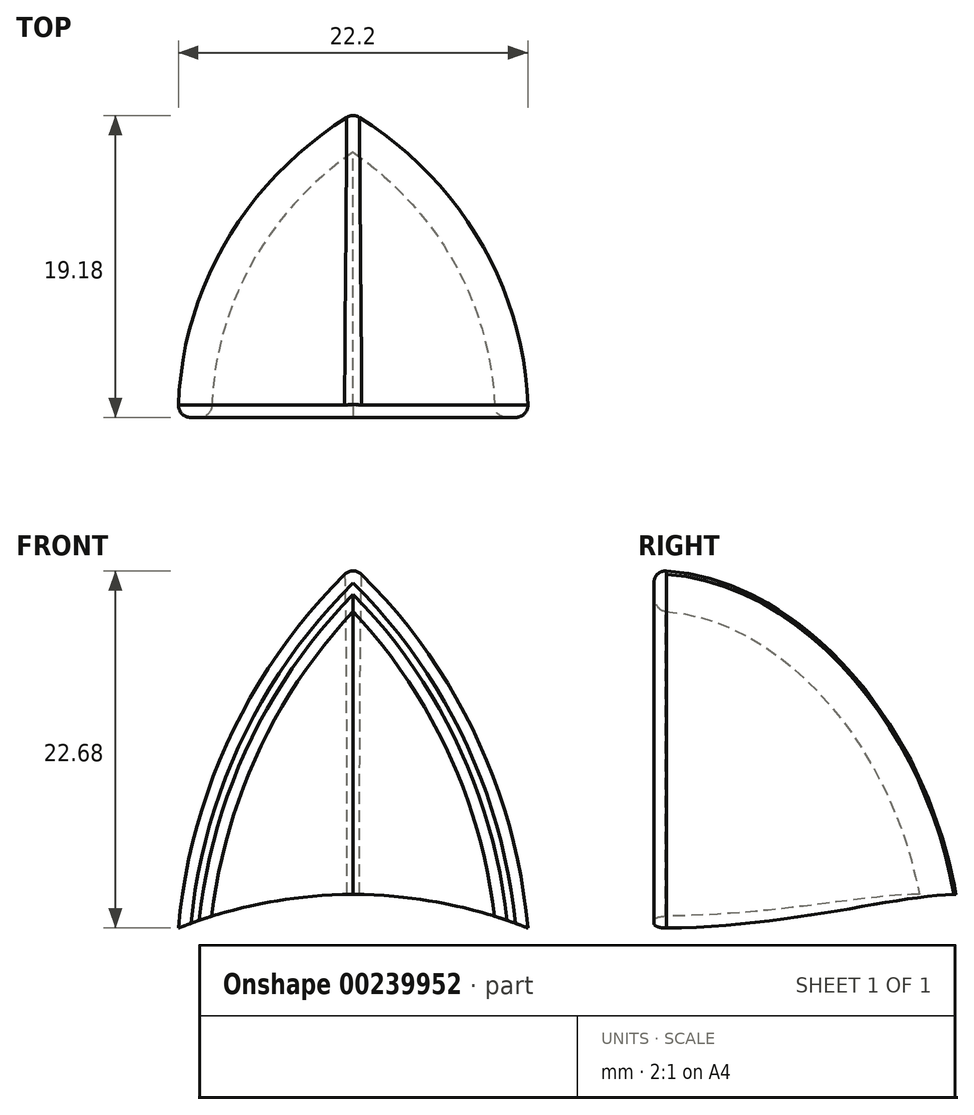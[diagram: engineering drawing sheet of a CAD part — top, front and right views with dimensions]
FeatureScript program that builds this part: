
annotation { "Feature Type Name" : "Feature", "Feature Type Description" : "" }
export const myFeature = defineFeature(function(context is Context, id is Id, definition is map)
    precondition{}
    {
        {
            var Q0;
            Q0=qCreatedBy(makeId("Front.planeOp"),FACE);
            var sketch = newSketch(context, id + "F0", { "sketchPlane" : qUnion([Q0])});
            skArc(sketch, "E0", {"start": v(22.86, 0) * mm, "mid": v(15.77, 18.5) * mm, "end": v(0, 30.48) * mm});
            skArc(sketch, "E1.0", {"start": v(20.82, 0) * mm, "mid": v(14.33, 17.03) * mm, "end": v(0, 28.29) * mm});
            skLineSegment(sketch, "E2", {"start": v(20.82, 0) * mm, "end": v(22.86, 0) * mm});
            skLineSegment(sketch, "E3", {"start": v(0, 28.29) * mm, "end": v(0, 30.48) * mm});
            skSolve(sketch);
        }
        {
            var Q0;
            Q0=makeQuery(id+"F0.imprint","IMPRINT",FACE,{"disambiguationData":[TD([[makeQuery(id+"F0.imprint","IMPRINT",EDGE,{"derivedFrom":sQuery(id+"F0.wireOp",EDGE,"E0")}),1.0]])]});
            var Q1;
            Q1=sQuery(id+"F0.wireOp",EDGE,"E3");
            revolve(context, id + "F1", {"entities" : qUnion([Q0]), "axis" : qUnion([Q1]), "revolveType" : RevolveType.ONE_DIRECTION, "angle" : 70 * degree});
        }
        {
            var Q0;
            Q0=makeQuery(id+"F1.opRevolve","CAP_FACE",FACE,{"disambiguationData":[OSD([sQuery(id+"F0.wireOp",EDGE,"E0"),sQuery(id+"F0.wireOp",EDGE,"E1.0"),sQuery(id+"F0.wireOp",EDGE,"E2"),sQuery(id+"F0.wireOp",EDGE,"E3")])],"isStart":true});
            var sketch = newSketch(context, id + "F2", { "sketchPlane" : qUnion([Q0])});
            skLineSegment(sketch, "E4.bottom", {"start": v(11.75, -2.07) * mm, "end": v(-2.53, -2.07) * mm});
            skLineSegment(sketch, "E4.top", {"start": v(11.75, 41.22) * mm, "end": v(-2.53, 41.22) * mm});
            skLineSegment(sketch, "E4.left", {"start": v(11.75, -2.07) * mm, "end": v(11.75, 41.22) * mm});
            skLineSegment(sketch, "E4.right", {"start": v(-2.53, -2.07) * mm, "end": v(-2.53, 41.22) * mm});
            skArc(sketch, "E5", {"start": v(22.86, 0) * mm, "mid": v(17.4, 1.6) * mm, "end": v(11.75, 2.15) * mm});
            skLineSegment(sketch, "E6", {"start": v(11.75, -2.07) * mm, "end": v(22.86, 0) * mm});
            skSolve(sketch);
        }
        {
            var Q0;
            {var subQ4=sQuery(id+"F2.wireOp",EDGE,"E4.bottom");Q0=makeQuery(id+"F2.imprint","IMPRINT",FACE,{"disambiguationData":[TD([[makeQuery(id+"F2.imprint","IMPRINT",EDGE,{"derivedFrom":subQ4}),-1.0]])]});}
            var Q1;
            {var subQ5=makeQuery(id+"F1.opRevolve","CAP_EDGE",EDGE,{"disambiguationData":[OSD([sQuery(id+"F0.wireOp",EDGE,"E3")])],"isStart":true});Q1=makeQuery(id+"F2.imprint","IMPRINT",FACE,{"disambiguationData":[TD([[makeQuery(id+"F2.imprint","IMPRINT",EDGE,{"derivedFrom":subQ5}),-1.0]])]});}
            var Q2;
            {var subQ1=sQuery(id+"F2.wireOp",EDGE,"E6");Q2=makeQuery(id+"F2.imprint","IMPRINT",FACE,{"disambiguationData":[TD([[makeQuery(id+"F2.imprint","IMPRINT",EDGE,{"derivedFrom":subQ1}),1.0]])]});}
            var Q3;
            {var subQ1=makeQuery(id+"F1.opRevolve","CAP_EDGE",EDGE,{"disambiguationData":[OSD([sQuery(id+"F0.wireOp",EDGE,"E2")])],"isStart":true});Q3=makeQuery(id+"F2.imprint","IMPRINT",FACE,{"disambiguationData":[TD([[makeQuery(id+"F2.imprint","IMPRINT",EDGE,{"derivedFrom":subQ1}),1.0]])]});}
            extrude(context, id + "F3", {"entities" : qUnion([Q0, Q1, Q2, Q3]), "operationType" : NewBodyOperationType.REMOVE, "endBound" : BoundingType.THROUGH_ALL, "oppositeDirection" : true, "depth" : 25.4 * mm});
        }
        {
            var Q0;
            Q0=makeQuery(id+"F1.opRevolve","SWEPT_BODY",BODY,{"disambiguationData":[OSD([sQuery(id+"F0.wireOp",EDGE,"E0"),sQuery(id+"F0.wireOp",EDGE,"E1.0"),sQuery(id+"F0.wireOp",EDGE,"E2"),sQuery(id+"F0.wireOp",EDGE,"E3")])]});
            var Q1;
            Q1=makeQuery(id+"F3.boolean.opBoolean","COPY",FACE,{"derivedFrom":makeQuery(id+"F3.opExtrude","SWEPT_FACE",FACE,{"disambiguationData":[OSD([sQuery(id+"F2.wireOp",EDGE,"E4.left")])]})});
            mirror(context, id + "F4", {"operationType" : NewBodyOperationType.ADD, "entities" : qUnion([Q0]), "mirrorPlane" : qUnion([Q1])});
        }
        {
            var Q0;
            {var subQ0=makeQuery(id+"F3.boolean.opBoolean","INTERSECT",EDGE,{"derivedFrom":[makeQuery(id+"F1.opRevolve","SWEPT_FACE",FACE,{"disambiguationData":[OSD([sQuery(id+"F0.wireOp",EDGE,"E0")])]}),makeQuery(id+"F3.opExtrude","SWEPT_FACE",FACE,{"disambiguationData":[OSD([sQuery(id+"F2.wireOp",EDGE,"E4.left")])]})]});Q0=makeQuery(id+"F4.boolean.opBoolean","MERGE",EDGE,{"derivedFrom":[subQ0,makeQuery(id+"F4.opPattern","COPY",EDGE,{"derivedFrom":subQ0,"instanceName":"1"})]});}
            var Q1;
            Q1=makeQuery(id+"F1.opRevolve","CAP_EDGE",EDGE,{"disambiguationData":[OSD([sQuery(id+"F0.wireOp",EDGE,"E0")])],"isStart":true});
            var Q2;
            Q2=makeQuery(id+"F4.opPattern","COPY",EDGE,{"derivedFrom":makeQuery(id+"F1.opRevolve","CAP_EDGE",EDGE,{"disambiguationData":[OSD([sQuery(id+"F0.wireOp",EDGE,"E0")])],"isStart":true}),"instanceName":"1"});
            var Q3;
            Q3=makeQuery(id+"F4.opPattern","COPY",EDGE,{"derivedFrom":makeQuery(id+"F1.opRevolve","CAP_EDGE",EDGE,{"disambiguationData":[OSD([sQuery(id+"F0.wireOp",EDGE,"E1.0")])],"isStart":true}),"instanceName":"1"});
            var Q4;
            Q4=makeQuery(id+"F1.opRevolve","CAP_EDGE",EDGE,{"disambiguationData":[OSD([sQuery(id+"F0.wireOp",EDGE,"E1.0")])],"isStart":true});
            fillet(context, id + "F5", {"entities" : qUnion([Q0, Q1, Q2, Q3, Q4]), "radius" : 0.76 * mm, "tangentPropagation" : true, "allowEdgeOverflow" : false});
        }
    });
